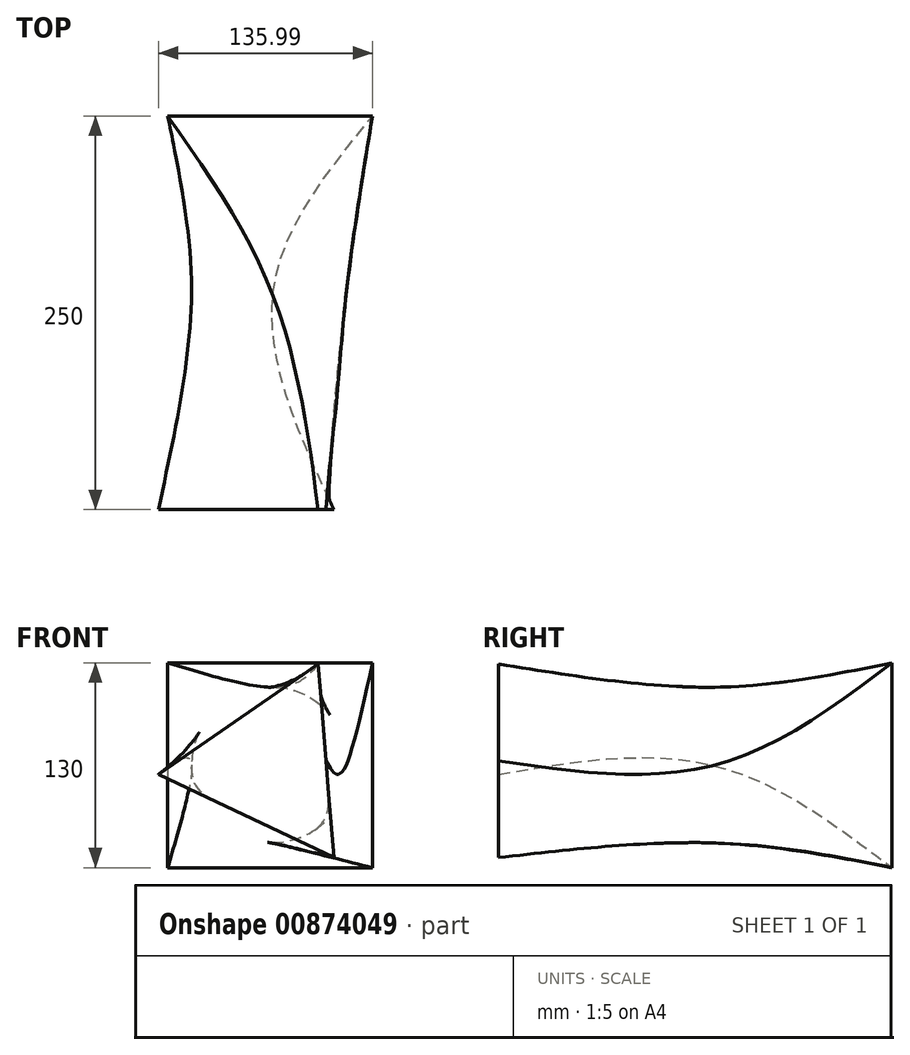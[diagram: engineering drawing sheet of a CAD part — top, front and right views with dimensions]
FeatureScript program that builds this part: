
annotation { "Feature Type Name" : "Feature", "Feature Type Description" : "" }
export const myFeature = defineFeature(function(context is Context, id is Id, definition is map)
    precondition{}
    {
        {
            var Q0;
            Q0=qCreatedBy(makeId("Front.planeOp"),FACE);
            cPlane(context, id + "F0", {"entities" : qUnion([Q0]), "cplaneType" : CPlaneType.OFFSET, "offset" : 100 * mm, "width" : 150 * mm, "height" : 150 * mm});
        }
        {
            var Q0;
            Q0=qCreatedBy(id+"F0.planeOp",FACE);
            var sketch = newSketch(context, id + "F1", { "sketchPlane" : qUnion([Q0])});
            skCircle(sketch, "E0", {"center": v(0, 0) * mm, "radius": 50 * mm});
            skSolve(sketch);
        }
        {
            var Q0;
            Q0=qCreatedBy(makeId("Front.planeOp"),FACE);
            var sketch = newSketch(context, id + "F2", { "sketchPlane" : qUnion([Q0])});
            skLineSegment(sketch, "E1.bottom", {"start": v(-65, 65) * mm, "end": v(65, 65) * mm});
            skLineSegment(sketch, "E1.top", {"start": v(-65, -65) * mm, "end": v(65, -65) * mm});
            skLineSegment(sketch, "E1.left", {"start": v(-65, 65) * mm, "end": v(-65, -65) * mm});
            skLineSegment(sketch, "E1.right", {"start": v(65, 65) * mm, "end": v(65, -65) * mm});
            skPoint(sketch, "E1.middle", {"position": v(0, 0) * mm});
            skSolve(sketch);
        }
        {
            var Q0;
            Q0=qCreatedBy(id+"F0.planeOp",FACE);
            cPlane(context, id + "F3", {"entities" : qUnion([Q0]), "cplaneType" : CPlaneType.OFFSET, "offset" : 150 * mm, "width" : 150 * mm, "height" : 150 * mm});
        }
        {
            var Q0;
            Q0=qCreatedBy(id+"F3.planeOp",FACE);
            var sketch = newSketch(context, id + "F4", { "sketchPlane" : qUnion([Q0])});
            skCircle(sketch, "E2.cCircle", {"center": v(0, 0) * mm, "radius": 35.61 * mm, "construction": true});
            skLineSegment(sketch, "E2.0", {"start": v(-70.99, -5.74) * mm, "end": v(30.52, 64.35) * mm});
            skLineSegment(sketch, "E2.1", {"start": v(30.52, 64.35) * mm, "end": v(40.46, -58.6) * mm});
            skLineSegment(sketch, "E2.2", {"start": v(40.46, -58.6) * mm, "end": v(-70.99, -5.74) * mm});
            skPoint(sketch, "E2.0.midPoint", {"position": v(-20.23, 29.3) * mm});
            skSolve(sketch);
        }
        {
            var Q0;
            Q0=makeQuery(id+"F4.imprint","IMPRINT",FACE,{"disambiguationData":[TD([[makeQuery(id+"F4.imprint","IMPRINT",EDGE,{"derivedFrom":sQuery(id+"F4.wireOp",EDGE,"E2.0")}),-1.0]])]});
            var Q1;
            Q1=makeQuery(id+"F1.imprint","IMPRINT",FACE,{"disambiguationData":[TD([[makeQuery(id+"F1.imprint","IMPRINT",EDGE,{"derivedFrom":sQuery(id+"F1.wireOp",EDGE,"E0")}),1.0]])]});
            var Q2;
            Q2=makeQuery(id+"F2.imprint","IMPRINT",FACE,{"disambiguationData":[TD([[makeQuery(id+"F2.imprint","IMPRINT",EDGE,{"derivedFrom":sQuery(id+"F2.wireOp",EDGE,"E1.bottom")}),-1.0]])]});
            loft(context, id + "F5", {"sheetProfilesArray" : [{ "sheetProfileEntities" : qUnion([Q0]) }, { "sheetProfileEntities" : qUnion([Q1]) }, { "sheetProfileEntities" : qUnion([Q2]) }]});
        }
    });
